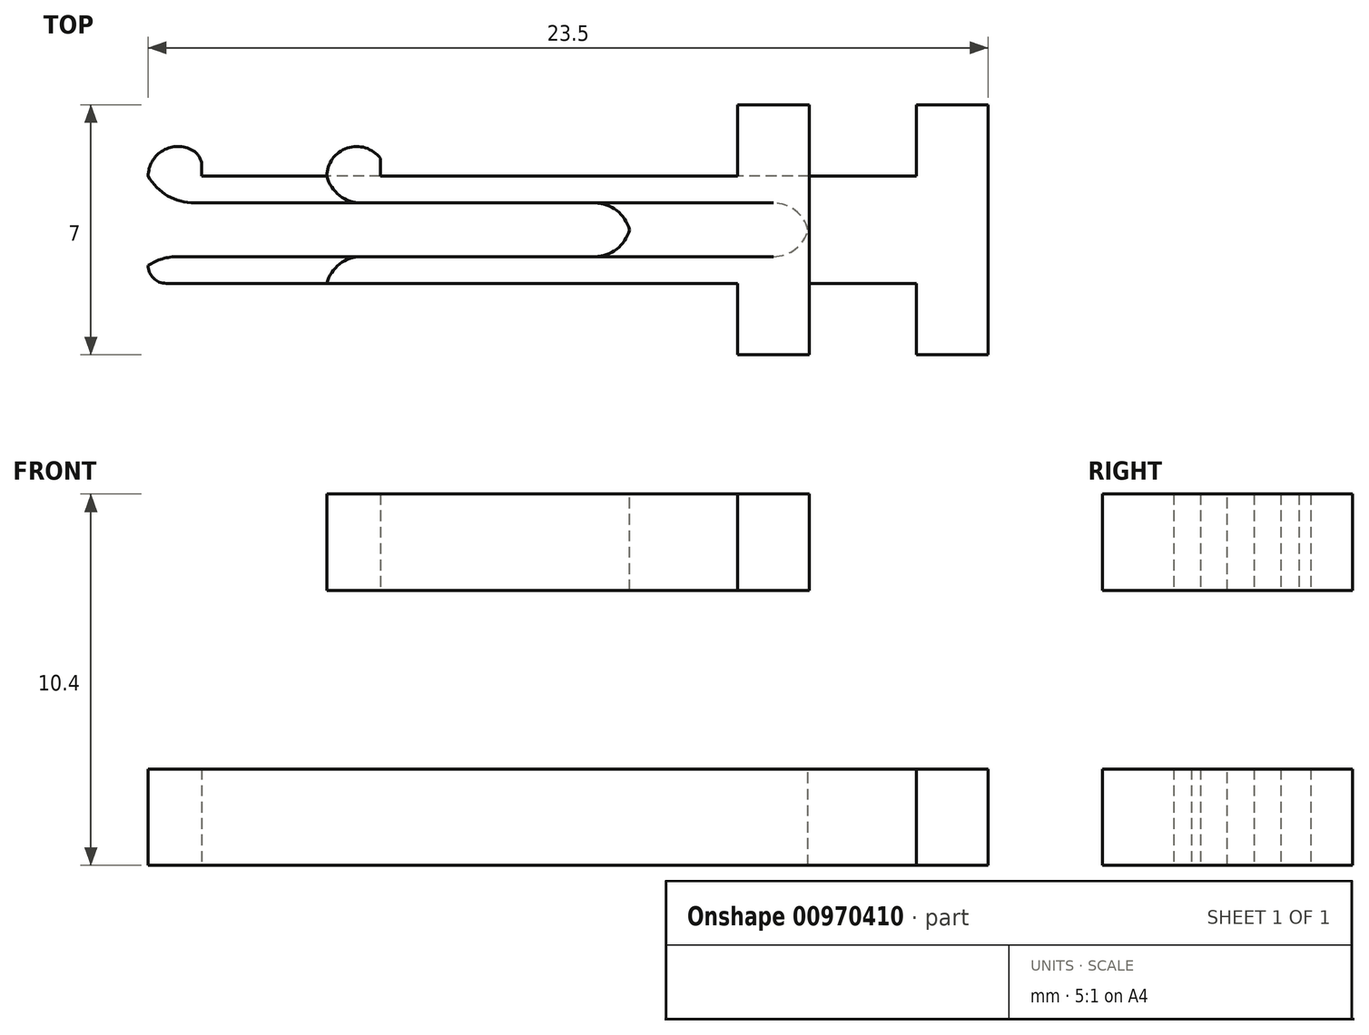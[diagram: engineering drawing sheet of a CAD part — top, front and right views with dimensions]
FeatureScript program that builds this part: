
annotation { "Feature Type Name" : "Feature", "Feature Type Description" : "" }
export const myFeature = defineFeature(function(context is Context, id is Id, definition is map)
    precondition{}
    {
        {
            var Q0;
            Q0=qCreatedBy(makeId("Top.planeOp"),FACE);
            var sketch = newSketch(context, id + "F0", { "sketchPlane" : qUnion([Q0])});
            skLineSegment(sketch, "E0", {"start": v(0, 1.5) * mm, "end": v(0, -1.5) * mm, "construction": true});
            skLineSegment(sketch, "E1.bottom", {"start": v(10.75, 1.5) * mm, "end": v(-10.75, 1.5) * mm});
            skLineSegment(sketch, "E1.top", {"start": v(10.75, -1.5) * mm, "end": v(-10.75, -1.5) * mm});
            skLineSegment(sketch, "E1.left", {"start": v(10.75, 1.5) * mm, "end": v(10.75, -1.5) * mm});
            skLineSegment(sketch, "E1.right", {"start": v(-10.75, 1.5) * mm, "end": v(-10.75, -1.5) * mm});
            skPoint(sketch, "E1.middle", {"position": v(0, 0) * mm});
            skLineSegment(sketch, "E2", {"start": v(0, 0) * mm, "end": v(-10.75, 0) * mm, "construction": true});
            skLineSegment(sketch, "E3.bottom", {"start": v(7.75, -0.75) * mm, "end": v(-18.5, -0.75) * mm});
            skLineSegment(sketch, "E3.top", {"start": v(7.75, 0.75) * mm, "end": v(-18.5, 0.75) * mm});
            skLineSegment(sketch, "E3.left", {"start": v(7.75, -0.75) * mm, "end": v(7.75, 0.75) * mm});
            skLineSegment(sketch, "E3.right", {"start": v(-18.5, -0.75) * mm, "end": v(-18.5, 0.75) * mm});
            skPoint(sketch, "E3.middle", {"position": v(-5.37, 0) * mm});
            skLineSegment(sketch, "E4", {"start": v(10.75, 1.5) * mm, "end": v(10.75, 3.5) * mm});
            skLineSegment(sketch, "E5", {"start": v(10.75, 3.5) * mm, "end": v(12.75, 3.5) * mm});
            skLineSegment(sketch, "E6", {"start": v(12.75, 3.5) * mm, "end": v(12.75, -3.5) * mm});
            skLineSegment(sketch, "E7", {"start": v(12.75, -3.5) * mm, "end": v(10.75, -3.5) * mm});
            skLineSegment(sketch, "E8", {"start": v(10.75, -3.5) * mm, "end": v(10.75, -1.5) * mm});
            skLineSegment(sketch, "E9", {"start": v(-10.75, 1.5) * mm, "end": v(-9.25, 1.5) * mm, "construction": true});
            skLineSegment(sketch, "E10", {"start": v(-9.25, 1.5) * mm, "end": v(-9.25, 2) * mm});
            skArc(sketch, "E11", {"start": v(-9.25, 2) * mm, "mid": v(-10.18, 2.3) * mm, "end": v(-10.75, 1.5) * mm});
            skLineSegment(sketch, "E12.MirrorCS", {"start": v(-18.5, 0) * mm, "end": v(-7.75, 0) * mm, "construction": true});
            skArc(sketch, "E13.MirrorCS", {"start": v(-9.25, -2) * mm, "mid": v(-10.18, -2.3) * mm, "end": v(-10.75, -1.5) * mm});
            skLineSegment(sketch, "E14.MirrorCS", {"start": v(-9.25, -1.5) * mm, "end": v(-9.25, -2) * mm});
            skLineSegment(sketch, "E15", {"start": v(-25.14, -10.12) * mm, "end": v(26.64, -10.12) * mm, "construction": true});
            skSolve(sketch);
        }
        {
            var Q0;
            {var subQ4=sQuery(id+"F0.wireOp",EDGE,"E1.left");Q0=makeQuery(id+"F0.imprint","IMPRINT",FACE,{"disambiguationData":[TD([[makeQuery(id+"F0.imprint","IMPRINT",EDGE,{"derivedFrom":subQ4}),-1.0]])]});}
            var Q1;
            Q1=makeQuery(id+"F0.imprint","IMPRINT",FACE,{"disambiguationData":[TD([[makeQuery(id+"F0.imprint","IMPRINT",EDGE,{"derivedFrom":sQuery(id+"F0.wireOp",EDGE,"E1.left")}),1.0]])]});
            var Q2;
            {var subQ2=sQuery(id+"F0.wireOp",EDGE,"E10");Q2=makeQuery(id+"F0.imprint","IMPRINT",FACE,{"disambiguationData":[TD([[makeQuery(id+"F0.imprint","IMPRINT",EDGE,{"derivedFrom":subQ2}),1.0]])]});}
            var Q3;
            {var subQ0=sQuery(id+"F0.wireOp",EDGE,"E13.MirrorCS");Q3=makeQuery(id+"F0.imprint","IMPRINT",FACE,{"disambiguationData":[TD([[makeQuery(id+"F0.imprint","IMPRINT",EDGE,{"derivedFrom":subQ0}),-1.0]])]});}
            extrude(context, id + "F1", {"entities" : qUnion([Q0, Q1, Q2, Q3]), "depth" : (3 - .3) * mm, "offsetDistance" : 25 * mm});
        }
        {
            var Q0;
            Q0=makeQuery(id+"F1.opExtrude","SWEPT_EDGE",EDGE,{"disambiguationData":[OSD([sQuery(id+"F0.wireOp",EDGE,"E10"),sQuery(id+"F0.wireOp",EDGE,"E11")])]});
            var Q1;
            Q1=makeQuery(id+"F1.opExtrude","SWEPT_EDGE",EDGE,{"disambiguationData":[OSD([sQuery(id+"F0.wireOp",EDGE,"E13.MirrorCS"),sQuery(id+"F0.wireOp",EDGE,"E14.MirrorCS")])]});
            fillet(context, id + "F2", {"entities" : qUnion([Q0, Q1]), "radius" : .5 * mm, "tangentPropagation" : true, "allowEdgeOverflow" : false});
        }
        {
            var Q0;
            Q0=makeQuery(id+"F1.opExtrude","SWEPT_EDGE",EDGE,{"disambiguationData":[OSD([sQuery(id+"F0.wireOp",EDGE,"E1.right"),sQuery(id+"F0.wireOp",EDGE,"E3.top")])]});
            var Q1;
            Q1=makeQuery(id+"F1.opExtrude","SWEPT_EDGE",EDGE,{"disambiguationData":[OSD([sQuery(id+"F0.wireOp",EDGE,"E1.right"),sQuery(id+"F0.wireOp",EDGE,"E3.bottom")])]});
            fillet(context, id + "F3", {"entities" : qUnion([Q0, Q1]), "radius" : 1.5 * mm, "tangentPropagation" : true, "allowEdgeOverflow" : false});
        }
        {
            var Q0;
            Q0=makeQuery(id+"F1.opExtrude","SWEPT_EDGE",EDGE,{"disambiguationData":[OSD([sQuery(id+"F0.wireOp",EDGE,"E3.top"),sQuery(id+"F0.wireOp",EDGE,"E3.left")])]});
            var Q1;
            Q1=makeQuery(id+"F1.opExtrude","SWEPT_EDGE",EDGE,{"disambiguationData":[OSD([sQuery(id+"F0.wireOp",EDGE,"E3.bottom"),sQuery(id+"F0.wireOp",EDGE,"E3.left")])]});
            fillet(context, id + "F4", {"entities" : qUnion([Q0, Q1]), "radius" : 1 * mm, "tangentPropagation" : true, "allowEdgeOverflow" : false});
        }
        {
            var Q0;
            Q0=makeQuery(id+"F1.opExtrude","CAP_FACE",FACE,{"disambiguationData":[OSD([sQuery(id+"F0.wireOp",EDGE,"E1.bottom"),sQuery(id+"F0.wireOp",EDGE,"E1.top"),sQuery(id+"F0.wireOp",EDGE,"E1.right"),sQuery(id+"F0.wireOp",EDGE,"E3.bottom"),sQuery(id+"F0.wireOp",EDGE,"E3.top"),sQuery(id+"F0.wireOp",EDGE,"E3.left"),sQuery(id+"F0.wireOp",EDGE,"E4"),sQuery(id+"F0.wireOp",EDGE,"E5"),sQuery(id+"F0.wireOp",EDGE,"E6"),sQuery(id+"F0.wireOp",EDGE,"E7"),sQuery(id+"F0.wireOp",EDGE,"E8"),sQuery(id+"F0.wireOp",EDGE,"E10"),sQuery(id+"F0.wireOp",EDGE,"E11"),sQuery(id+"F0.wireOp",EDGE,"E13.MirrorCS"),sQuery(id+"F0.wireOp",EDGE,"E14.MirrorCS")])],"isStart":false});
            cPlane(context, id + "F5", {"entities" : qUnion([Q0]), "cplaneType" : CPlaneType.OFFSET, "offset" : 5 * mm, "width" : 150 * mm, "height" : 150 * mm});
        }
        {
            var Q0;
            Q0=qCreatedBy(id+"F5.planeOp",FACE);
            var sketch = newSketch(context, id + "F6", { "sketchPlane" : qUnion([Q0])});
            skLineSegment(sketch, "E16", {"start": v(1.48, 1.5) * mm, "end": v(1.48, -1.5) * mm, "construction": true});
            skLineSegment(sketch, "E17.bottom", {"start": v(5.75, 1.5) * mm, "end": v(-5.75, 1.5) * mm});
            skLineSegment(sketch, "E17.top", {"start": v(5.75, -1.5) * mm, "end": v(-5.75, -1.5) * mm});
            skLineSegment(sketch, "E17.left", {"start": v(5.75, 1.5) * mm, "end": v(5.75, -1.5) * mm});
            skLineSegment(sketch, "E17.right", {"start": v(-5.75, 1.5) * mm, "end": v(-5.75, -1.5) * mm});
            skPoint(sketch, "E17.middle", {"position": v(0, 0) * mm});
            skLineSegment(sketch, "E18", {"start": v(0, 0) * mm, "end": v(-5.75, 0) * mm, "construction": true});
            skLineSegment(sketch, "E19.bottom", {"start": v(2.75, -0.75) * mm, "end": v(-8.5, -0.75) * mm});
            skLineSegment(sketch, "E19.top", {"start": v(2.75, 0.75) * mm, "end": v(-8.5, 0.75) * mm});
            skLineSegment(sketch, "E19.left", {"start": v(2.75, -0.75) * mm, "end": v(2.75, 0.75) * mm});
            skLineSegment(sketch, "E19.right", {"start": v(-8.5, -0.75) * mm, "end": v(-8.5, 0.75) * mm});
            skPoint(sketch, "E19.middle", {"position": v(-2.88, 0) * mm});
            skLineSegment(sketch, "E20", {"start": v(5.75, 1.5) * mm, "end": v(5.75, 3.5) * mm});
            skLineSegment(sketch, "E21", {"start": v(5.75, 3.5) * mm, "end": v(7.75, 3.5) * mm});
            skLineSegment(sketch, "E22", {"start": v(7.75, 3.5) * mm, "end": v(7.75, -3.5) * mm});
            skLineSegment(sketch, "E23", {"start": v(7.75, -3.5) * mm, "end": v(5.75, -3.5) * mm});
            skLineSegment(sketch, "E24", {"start": v(5.75, -3.5) * mm, "end": v(5.75, -1.5) * mm});
            skLineSegment(sketch, "E25", {"start": v(-5.75, 1.5) * mm, "end": v(-4.25, 1.5) * mm, "construction": true});
            skLineSegment(sketch, "E26", {"start": v(-4.25, 1.5) * mm, "end": v(-4.25, 2) * mm});
            skArc(sketch, "E27", {"start": v(-4.25, 2) * mm, "mid": v(-5.18, 2.3) * mm, "end": v(-5.75, 1.5) * mm});
            skLineSegment(sketch, "E28.MirrorCS", {"start": v(-8.5, 0) * mm, "end": v(-2.75, 0) * mm, "construction": true});
            skArc(sketch, "E29.MirrorCS", {"start": v(-4.25, -2) * mm, "mid": v(-5.18, -2.3) * mm, "end": v(-5.75, -1.5) * mm});
            skLineSegment(sketch, "E30.MirrorCS", {"start": v(-4.25, -1.5) * mm, "end": v(-4.25, -2) * mm});
            skLineSegment(sketch, "E31", {"start": v(-25.14, -10.12) * mm, "end": v(26.64, -10.12) * mm, "construction": true});
            skSolve(sketch);
        }
        {
            var Q0;
            Q0=makeQuery(id+"F6.imprint","IMPRINT",FACE,{"disambiguationData":[TD([[makeQuery(id+"F6.imprint","IMPRINT",EDGE,{"derivedFrom":sQuery(id+"F6.wireOp",EDGE,"E17.left")}),1.0]])]});
            var Q1;
            {var subQ4=sQuery(id+"F6.wireOp",EDGE,"E17.left");Q1=makeQuery(id+"F6.imprint","IMPRINT",FACE,{"disambiguationData":[TD([[makeQuery(id+"F6.imprint","IMPRINT",EDGE,{"derivedFrom":subQ4}),-1.0]])]});}
            var Q2;
            {var subQ2=sQuery(id+"F6.wireOp",EDGE,"E26");Q2=makeQuery(id+"F6.imprint","IMPRINT",FACE,{"disambiguationData":[TD([[makeQuery(id+"F6.imprint","IMPRINT",EDGE,{"derivedFrom":subQ2}),1.0]])]});}
            var Q3;
            {var subQ0=sQuery(id+"F6.wireOp",EDGE,"E29.MirrorCS");Q3=makeQuery(id+"F6.imprint","IMPRINT",FACE,{"disambiguationData":[TD([[makeQuery(id+"F6.imprint","IMPRINT",EDGE,{"derivedFrom":subQ0}),-1.0]])]});}
            extrude(context, id + "F7", {"entities" : qUnion([Q0, Q1, Q2, Q3]), "depth" : 2.7 * mm, "offsetDistance" : 25 * mm});
        }
        {
            var Q0;
            Q0=makeQuery(id+"F7.opExtrude","SWEPT_EDGE",EDGE,{"disambiguationData":[OSD([sQuery(id+"F6.wireOp",EDGE,"E17.right"),sQuery(id+"F6.wireOp",EDGE,"E19.top")])]});
            var Q1;
            Q1=makeQuery(id+"F7.opExtrude","SWEPT_EDGE",EDGE,{"disambiguationData":[OSD([sQuery(id+"F6.wireOp",EDGE,"E17.right"),sQuery(id+"F6.wireOp",EDGE,"E19.bottom")])]});
            fillet(context, id + "F8", {"entities" : qUnion([Q0, Q1]), "radius" : 1 * mm, "tangentPropagation" : true, "allowEdgeOverflow" : false});
        }
        {
            var Q0;
            Q0=makeQuery(id+"F7.opExtrude","SWEPT_EDGE",EDGE,{"disambiguationData":[OSD([sQuery(id+"F6.wireOp",EDGE,"E19.top"),sQuery(id+"F6.wireOp",EDGE,"E19.left")])]});
            var Q1;
            Q1=makeQuery(id+"F7.opExtrude","SWEPT_EDGE",EDGE,{"disambiguationData":[OSD([sQuery(id+"F6.wireOp",EDGE,"E19.bottom"),sQuery(id+"F6.wireOp",EDGE,"E19.left")])]});
            fillet(context, id + "F9", {"entities" : qUnion([Q0, Q1]), "radius" : 1 * mm, "tangentPropagation" : true, "allowEdgeOverflow" : false});
        }
    });
